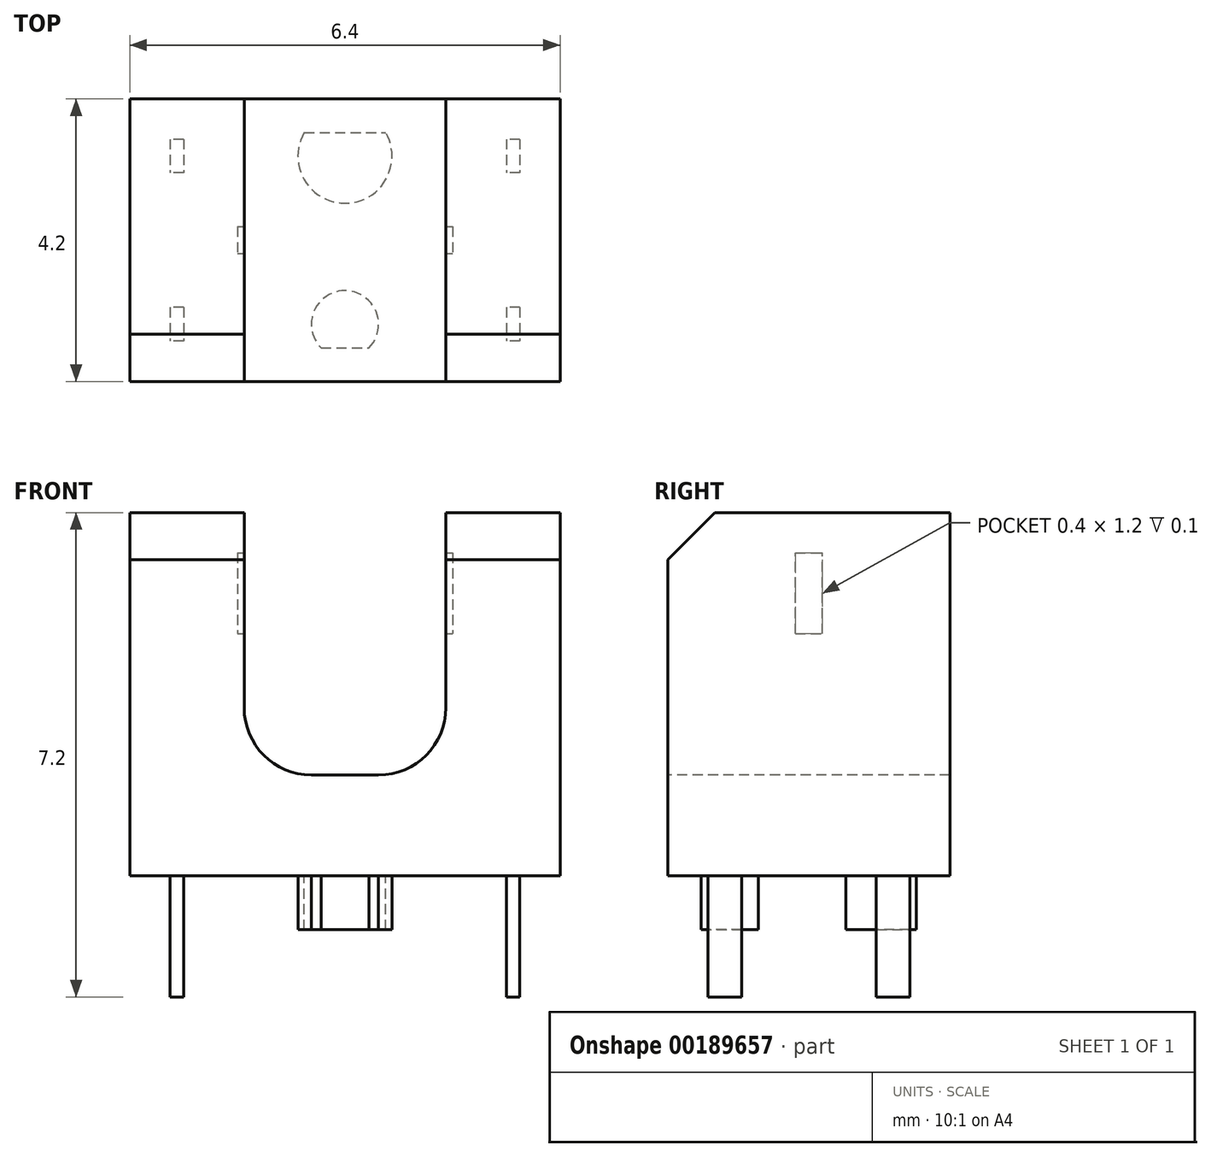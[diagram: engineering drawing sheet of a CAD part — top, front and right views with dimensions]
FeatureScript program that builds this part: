
annotation { "Feature Type Name" : "Feature", "Feature Type Description" : "" }
export const myFeature = defineFeature(function(context is Context, id is Id, definition is map)
    precondition{}
    {
        {
            var Q0;
            Q0=qCreatedBy(makeId("Top.planeOp"),FACE);
            var sketch = newSketch(context, id + "F0", { "sketchPlane" : qUnion([Q0])});
            skLineSegment(sketch, "E0.rect.bottom", {"start": v(3.2, 2.1) * mm, "end": v(-3.2, 2.1) * mm});
            skLineSegment(sketch, "E0.rect.top", {"start": v(3.2, -2.1) * mm, "end": v(-3.2, -2.1) * mm});
            skLineSegment(sketch, "E0.rect.left", {"start": v(3.2, 2.1) * mm, "end": v(3.2, -2.1) * mm});
            skLineSegment(sketch, "E0.rect.right", {"start": v(-3.2, 2.1) * mm, "end": v(-3.2, -2.1) * mm});
            skPoint(sketch, "E0.rect.middle", {"position": v(0, 0) * mm});
            skSolve(sketch);
        }
        {
            var Q0;
            Q0=qSketchRegion(id+"F0",true);
            extrude(context, id + "F1", {"entities" : qUnion([Q0]), "depth" : 5.4 * mm});
        }
        {
            var Q0;
            Q0=makeQuery(id+"F1.opExtrude","SWEPT_FACE",FACE,{"disambiguationData":[OSD([sQuery(id+"F0.wireOp",EDGE,"E0.rect.top")])]});
            var sketch = newSketch(context, id + "F2", { "sketchPlane" : qUnion([Q0])});
            skLineSegment(sketch, "E1.rect.bottom", {"start": v(1.5, 5.4) * mm, "end": v(-1.5, 5.4) * mm});
            skLineSegment(sketch, "E1.rect.top", {"start": v(0.5, 1.5) * mm, "end": v(-0.5, 1.5) * mm});
            skLineSegment(sketch, "E1.rect.left", {"start": v(1.5, 5.4) * mm, "end": v(1.5, 2.5) * mm});
            skLineSegment(sketch, "E1.rect.right", {"start": v(-1.5, 5.4) * mm, "end": v(-1.5, 2.5) * mm});
            skPoint(sketch, "E1.rect.middle", {"position": v(0, 3.45) * mm});
            skPoint(sketch, "E2.visualSharp", {"position": v(-1.5, 1.5) * mm});
            skArc(sketch, "E2.filletArc", {"start": v(-1.5, 2.5) * mm, "mid": v(-1.2, 1.8) * mm, "end": v(-0.5, 1.5) * mm});
            skPoint(sketch, "E3.visualSharp", {"position": v(1.5, 1.5) * mm});
            skArc(sketch, "E3.filletArc", {"start": v(0.5, 1.5) * mm, "mid": v(1.2, 1.8) * mm, "end": v(1.5, 2.5) * mm});
            skSolve(sketch);
        }
        {
            var Q0;
            Q0=qSketchRegion(id+"F2",true);
            var Q1;
            Q1=makeQuery(id+"F1.opExtrude","SWEPT_FACE",FACE,{"disambiguationData":[OSD([sQuery(id+"F0.wireOp",EDGE,"E0.rect.bottom")])]});
            extrude(context, id + "F3", {"entities" : qUnion([Q0]), "operationType" : NewBodyOperationType.REMOVE, "endBound" : BoundingType.UP_TO_SURFACE, "oppositeDirection" : true, "endBoundEntityFace" : qUnion([Q1]), "depth" : 25 * mm});
        }
        {
            var Q0;
            {var subQ0=sQuery(id+"F0.wireOp",EDGE,"E0.rect.right");var subQ1=sQuery(id+"F0.wireOp",EDGE,"E0.rect.top");Q0=makeQuery(id+"F3.boolean.opBoolean","SPLIT",EDGE,{"disambiguationData":[TD([makeQuery(id+"F1.opExtrude","SWEPT_FACE",FACE,{"disambiguationData":[OSD([subQ0])]})])],"derivedFrom":makeQuery(id+"F1.opExtrude","CAP_EDGE",EDGE,{"disambiguationData":[OSD([subQ1])],"isStart":false})});}
            var Q1;
            {var subQ0=sQuery(id+"F0.wireOp",EDGE,"E0.rect.left");var subQ1=sQuery(id+"F0.wireOp",EDGE,"E0.rect.top");Q1=makeQuery(id+"F3.boolean.opBoolean","SPLIT",EDGE,{"disambiguationData":[TD([makeQuery(id+"F1.opExtrude","SWEPT_FACE",FACE,{"disambiguationData":[OSD([subQ0])]})])],"derivedFrom":makeQuery(id+"F1.opExtrude","CAP_EDGE",EDGE,{"disambiguationData":[OSD([subQ1])],"isStart":false})});}
            chamfer(context, id + "F4", {"entities" : qUnion([Q0, Q1]), "width" : 0.7 * mm, "tangentPropagation" : true});
        }
        {
            var Q0;
            Q0=qCreatedBy(makeId("Right.planeOp"),FACE);
            var sketch = newSketch(context, id + "F5", { "sketchPlane" : qUnion([Q0])});
            skLineSegment(sketch, "E4.rect.bottom", {"start": v(0.2, 4.8) * mm, "end": v(-0.2, 4.8) * mm});
            skLineSegment(sketch, "E4.rect.top", {"start": v(0.2, 3.6) * mm, "end": v(-0.2, 3.6) * mm});
            skLineSegment(sketch, "E4.rect.left", {"start": v(0.2, 4.8) * mm, "end": v(0.2, 3.6) * mm});
            skLineSegment(sketch, "E4.rect.right", {"start": v(-0.2, 4.8) * mm, "end": v(-0.2, 3.6) * mm});
            skPoint(sketch, "E4.rect.middle", {"position": v(0, 4.2) * mm});
            skSolve(sketch);
        }
        {
            var Q0;
            Q0=qSketchRegion(id+"F5",true);
            extrude(context, id + "F6", {"entities" : qUnion([Q0]), "operationType" : NewBodyOperationType.REMOVE, "oppositeDirection" : true, "depth" : 3.2 * mm, "symmetric" : true});
        }
        {
            var Q0;
            Q0=makeQuery(id+"F1.opExtrude","CAP_FACE",FACE,{"disambiguationData":[OSD([sQuery(id+"F0.wireOp",EDGE,"E0.rect.bottom"),sQuery(id+"F0.wireOp",EDGE,"E0.rect.top"),sQuery(id+"F0.wireOp",EDGE,"E0.rect.left"),sQuery(id+"F0.wireOp",EDGE,"E0.rect.right")])],"isStart":true});
            var sketch = newSketch(context, id + "F7", { "sketchPlane" : qUnion([Q0])});
            skArc(sketch, "E5", {"start": v(-0.36, 1.6) * mm, "mid": v(0, 0.75) * mm, "end": v(0.36, 1.6) * mm});
            skArc(sketch, "E6", {"start": v(0.6, -1.6) * mm, "mid": v(0, -0.55) * mm, "end": v(-0.6, -1.6) * mm});
            skLineSegment(sketch, "E7", {"start": v(-0.36, 1.6) * mm, "end": v(0.36, 1.6) * mm});
            skLineSegment(sketch, "E8", {"start": v(-0.6, -1.6) * mm, "end": v(0.6, -1.6) * mm});
            skSolve(sketch);
        }
        {
            var Q0;
            Q0=qSketchRegion(id+"F7",true);
            extrude(context, id + "F8", {"entities" : qUnion([Q0]), "operationType" : NewBodyOperationType.ADD, "depth" : 0.8 * mm});
        }
        {
            var Q0;
            Q0=makeQuery(id+"F1.opExtrude","CAP_FACE",FACE,{"disambiguationData":[OSD([sQuery(id+"F0.wireOp",EDGE,"E0.rect.bottom"),sQuery(id+"F0.wireOp",EDGE,"E0.rect.top"),sQuery(id+"F0.wireOp",EDGE,"E0.rect.left"),sQuery(id+"F0.wireOp",EDGE,"E0.rect.right")])],"isStart":true});
            var sketch = newSketch(context, id + "F9", { "sketchPlane" : qUnion([Q0])});
            skLineSegment(sketch, "E9.rect.bottom", {"start": v(-2.4, 1) * mm, "end": v(-2.6, 1) * mm});
            skLineSegment(sketch, "E9.rect.top", {"start": v(-2.4, 1.5) * mm, "end": v(-2.6, 1.5) * mm});
            skLineSegment(sketch, "E9.rect.left", {"start": v(-2.4, 1) * mm, "end": v(-2.4, 1.5) * mm});
            skLineSegment(sketch, "E9.rect.right", {"start": v(-2.6, 1) * mm, "end": v(-2.6, 1.5) * mm});
            skPoint(sketch, "E9.rect.middle", {"position": v(-2.5, 1.25) * mm});
            skLineSegment(sketch, "E10.0.1.0", {"start": v(-2.6, -1.5) * mm, "end": v(-2.6, -1) * mm});
            skLineSegment(sketch, "E10.0.1.1", {"start": v(-2.4, -1.5) * mm, "end": v(-2.6, -1.5) * mm});
            skLineSegment(sketch, "E10.0.1.2", {"start": v(-2.4, -1.5) * mm, "end": v(-2.4, -1) * mm});
            skLineSegment(sketch, "E10.0.1.3", {"start": v(-2.4, -1) * mm, "end": v(-2.6, -1) * mm});
            skPoint(sketch, "E10.0.1.4", {"position": v(-2.5, -1.25) * mm});
            skLineSegment(sketch, "E10.1.0.0", {"start": v(2.4, 1) * mm, "end": v(2.4, 1.5) * mm});
            skLineSegment(sketch, "E10.1.0.1", {"start": v(2.6, 1) * mm, "end": v(2.4, 1) * mm});
            skLineSegment(sketch, "E10.1.0.2", {"start": v(2.6, 1) * mm, "end": v(2.6, 1.5) * mm});
            skLineSegment(sketch, "E10.1.0.3", {"start": v(2.6, 1.5) * mm, "end": v(2.4, 1.5) * mm});
            skPoint(sketch, "E10.1.0.4", {"position": v(2.5, 1.25) * mm});
            skLineSegment(sketch, "E10.1.1.0", {"start": v(2.4, -1.5) * mm, "end": v(2.4, -1) * mm});
            skLineSegment(sketch, "E10.1.1.1", {"start": v(2.6, -1.5) * mm, "end": v(2.4, -1.5) * mm});
            skLineSegment(sketch, "E10.1.1.2", {"start": v(2.6, -1.5) * mm, "end": v(2.6, -1) * mm});
            skLineSegment(sketch, "E10.1.1.3", {"start": v(2.6, -1) * mm, "end": v(2.4, -1) * mm});
            skPoint(sketch, "E10.1.1.4", {"position": v(2.5, -1.25) * mm});
            skLineSegment(sketch, "E10.direction1", {"start": v(-2.6, 1) * mm, "end": v(2.4, 1) * mm, "construction": true});
            skLineSegment(sketch, "E10.direction2", {"start": v(-2.6, 1) * mm, "end": v(-2.6, -1.5) * mm, "construction": true});
            skSolve(sketch);
        }
        {
            var Q0;
            Q0=qSketchRegion(id+"F9",true);
            extrude(context, id + "F10", {"entities" : qUnion([Q0]), "operationType" : NewBodyOperationType.ADD, "depth" : 1.8 * mm});
        }
    });
